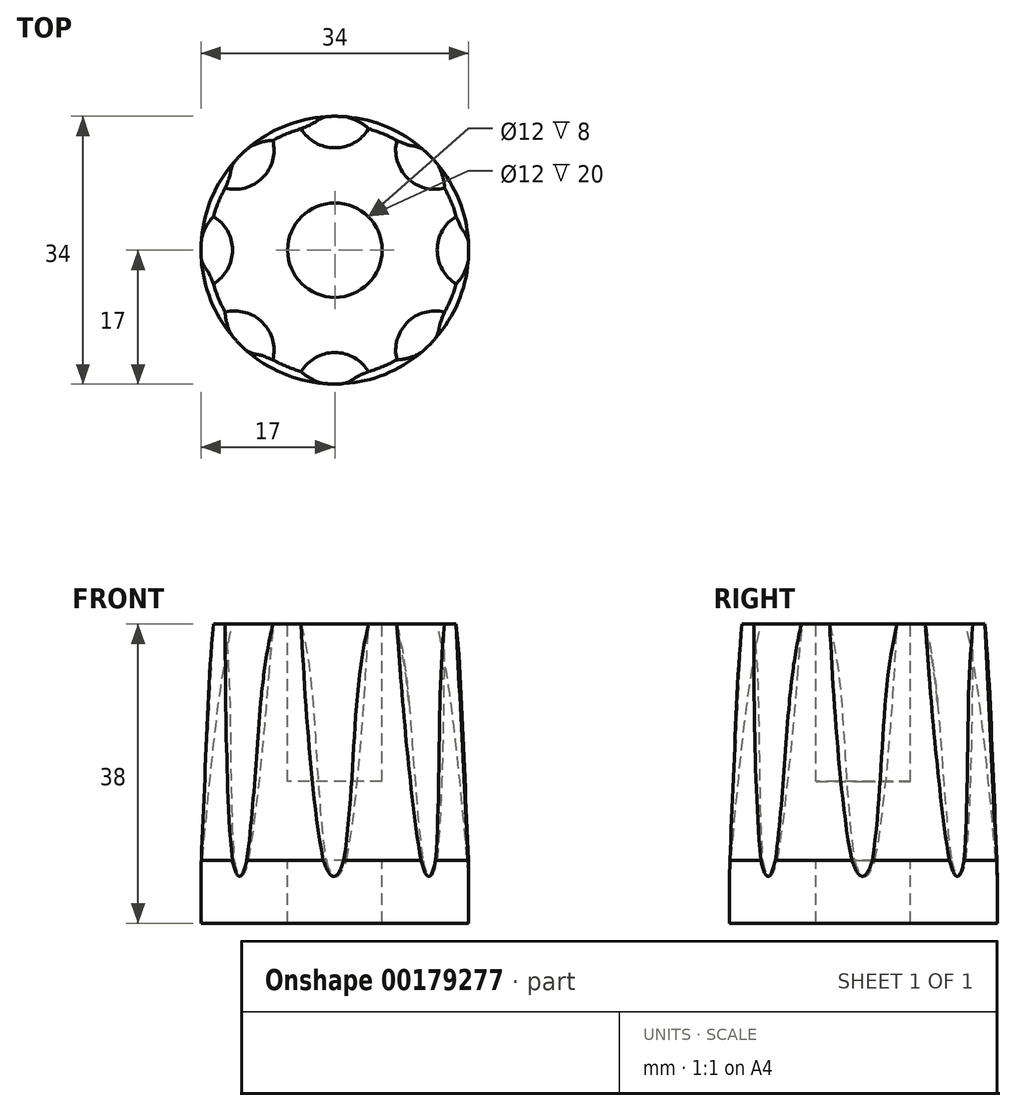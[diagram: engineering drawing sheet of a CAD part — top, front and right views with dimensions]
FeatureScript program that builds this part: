
annotation { "Feature Type Name" : "Feature", "Feature Type Description" : "" }
export const myFeature = defineFeature(function(context is Context, id is Id, definition is map)
    precondition{}
    {
        {
            var Q0;
            Q0=qCreatedBy(makeId("Front.planeOp"),FACE);
            var sketch = newSketch(context, id + "F0", { "sketchPlane" : qUnion([Q0])});
            skLineSegment(sketch, "E0", {"start": v(0, 8) * mm, "end": v(6, 8) * mm});
            skLineSegment(sketch, "E1", {"start": v(6, 8) * mm, "end": v(6, 0) * mm});
            skLineSegment(sketch, "E2", {"start": v(6, 0) * mm, "end": v(17, 0) * mm});
            skLineSegment(sketch, "E3", {"start": v(17, 0) * mm, "end": v(17, 8) * mm});
            skLineSegment(sketch, "E4", {"start": v(17, 8) * mm, "end": v(16, 38) * mm});
            skLineSegment(sketch, "E5", {"start": v(16, 38) * mm, "end": v(0, 38) * mm});
            skLineSegment(sketch, "E6", {"start": v(0, 38) * mm, "end": v(0, 8) * mm});
            skSolve(sketch);
        }
        {
            var Q0;
            Q0=makeQuery(id+"F0.imprint","IMPRINT",FACE,{"disambiguationData":[TD([[makeQuery(id+"F0.imprint","IMPRINT",EDGE,{"derivedFrom":sQuery(id+"F0.wireOp",EDGE,"E0")}),1.0]])]});
            var Q1;
            Q1=sQuery(id+"F0.wireOp",EDGE,"E6");
            revolve(context, id + "F1", {"entities" : qUnion([Q0]), "axis" : qUnion([Q1]), "revolveType" : RevolveType.FULL});
        }
        {
            var Q0;
            Q0=makeQuery(id+"F1.opRevolve","SWEPT_FACE",FACE,{"disambiguationData":[OSD([sQuery(id+"F0.wireOp",EDGE,"E5")])]});
            var sketch = newSketch(context, id + "F2", { "sketchPlane" : qUnion([Q0])});
            skCircle(sketch, "E7", {"center": v(18, 0) * mm, "radius": 5 * mm});
            skCircle(sketch, "E8.1.0", {"center": v(12.73, 12.73) * mm, "radius": 5 * mm});
            skCircle(sketch, "E8.2.0", {"center": v(0, 18) * mm, "radius": 5 * mm});
            skCircle(sketch, "E8.3.0", {"center": v(-12.73, 12.73) * mm, "radius": 5 * mm});
            skCircle(sketch, "E8.4.0", {"center": v(-18, 0) * mm, "radius": 5 * mm});
            skCircle(sketch, "E8.5.0", {"center": v(-12.73, -12.73) * mm, "radius": 5 * mm});
            skCircle(sketch, "E8.6.0", {"center": v(0, -18) * mm, "radius": 5 * mm});
            skCircle(sketch, "E8.7.0", {"center": v(12.73, -12.73) * mm, "radius": 5 * mm});
            skPoint(sketch, "E8.center", {"position": v(0, 0) * mm});
            skSolve(sketch);
        }
        {
            var Q0;
            Q0=makeQuery(id+"F1.opRevolve","SWEPT_FACE",FACE,{"disambiguationData":[OSD([sQuery(id+"F0.wireOp",EDGE,"E2")])]});
            var sketch = newSketch(context, id + "F3", { "sketchPlane" : qUnion([Q0])});
            skCircle(sketch, "E9", {"center": v(0, -25) * mm, "radius": 7.5 * mm});
            skCircle(sketch, "E10.1.0", {"center": v(17.68, -17.68) * mm, "radius": 7.5 * mm});
            skCircle(sketch, "E10.2.0", {"center": v(25, 0) * mm, "radius": 7.5 * mm});
            skCircle(sketch, "E10.3.0", {"center": v(17.68, 17.68) * mm, "radius": 7.5 * mm});
            skCircle(sketch, "E10.4.0", {"center": v(0, 25) * mm, "radius": 7.5 * mm});
            skCircle(sketch, "E10.5.0", {"center": v(-17.68, 17.68) * mm, "radius": 7.5 * mm});
            skCircle(sketch, "E10.6.0", {"center": v(-25, 0) * mm, "radius": 7.5 * mm});
            skCircle(sketch, "E10.7.0", {"center": v(-17.68, -17.68) * mm, "radius": 7.5 * mm});
            skPoint(sketch, "E10.center", {"position": v(0, 0) * mm});
            skSolve(sketch);
        }
        {
            var Q1;
            {var subQ0=sQuery(id+"F2.wireOp",EDGE,"E7");var subQ1=makeQuery(id+"F1.opRevolve","SWEPT_EDGE",EDGE,{"disambiguationData":[OSD([sQuery(id+"F0.wireOp",EDGE,"E4"),sQuery(id+"F0.wireOp",EDGE,"E5")])]});var subQ2=makeQuery(id+"F2.imprint","INTERSECT",VERTEX,{"disambiguationData":[OD(0.0)],"derivedFrom":[subQ1,subQ0]});Q1=makeQuery(id+"F2.imprint","IMPRINT",FACE,{"disambiguationData":[TD([[makeQuery(id+"F2.imprint","IMPRINT",EDGE,{"disambiguationData":[TD([[subQ2,1.0]])],"derivedFrom":subQ0}),1.0]])]});}
            var Q2;
            Q2=makeQuery(id+"F3.imprint","IMPRINT",FACE,{"disambiguationData":[TD([[makeQuery(id+"F3.imprint","IMPRINT",EDGE,{"derivedFrom":sQuery(id+"F3.wireOp",EDGE,"E10.2.0")}),1.0]])]});
            loft(context, id + "F4", {"sheetProfilesArray" : [{ "sheetProfileEntities" : qUnion([Q1]) }, { "sheetProfileEntities" : qUnion([Q2]) }]});
        }
        {
            var Q0;
            {var subQ0=sQuery(id+"F2.wireOp",EDGE,"E7");var subQ1=makeQuery(id+"F1.opRevolve","SWEPT_EDGE",EDGE,{"disambiguationData":[OSD([sQuery(id+"F0.wireOp",EDGE,"E4"),sQuery(id+"F0.wireOp",EDGE,"E5")])]});var subQ2=makeQuery(id+"F2.imprint","INTERSECT",VERTEX,{"disambiguationData":[OD(0.0)],"derivedFrom":[subQ1,subQ0]});Q0=makeQuery(id+"F4.opLoft","SWEPT_BODY",BODY,{"disambiguationData":[OSD([makeQuery(id+"F2.imprint","IMPRINT",FACE,{"disambiguationData":[TD([[makeQuery(id+"F2.imprint","IMPRINT",EDGE,{"disambiguationData":[TD([[subQ2,1.0]])],"derivedFrom":subQ0}),1.0]])]}),makeQuery(id+"F3.imprint","IMPRINT",FACE,{"disambiguationData":[TD([[makeQuery(id+"F3.imprint","IMPRINT",EDGE,{"derivedFrom":sQuery(id+"F3.wireOp",EDGE,"E10.2.0")}),1.0]])]})])]});}
            var Q1;
            Q1=sQuery(id+"F0.wireOp",EDGE,"E6");
            circularPattern(context, id + "F5", {"operationType" : NewBodyOperationType.REMOVE, "entities" : qUnion([Q0]), "axis" : qUnion([Q1]), "angle" : 45 * degree, "instanceCount" : 8});
        }
        {
            var Q0;
            Q0=makeQuery(id+"F1.opRevolve","SWEPT_FACE",FACE,{"disambiguationData":[OSD([sQuery(id+"F0.wireOp",EDGE,"E5")])]});
            var sketch = newSketch(context, id + "F6", { "sketchPlane" : qUnion([Q0])});
            skCircle(sketch, "E11", {"center": v(0, 0) * mm, "radius": 6 * mm});
            skFitSpline(sketch, "E12.0", {"points": [v(-13.93, -7.87) * mm, v(-13.72, -7.82) * mm, v(-13.5, -7.78) * mm, v(-13.3, -7.76) * mm, v(-13.08, -7.74) * mm, v(-12.87, -7.73) * mm, v(-12.66, -7.73) * mm, v(-12.44, -7.73) * mm, v(-12.23, -7.75) * mm, v(-12.02, -7.78) * mm, v(-11.8, -7.8) * mm, v(-11.6, -7.85) * mm, v(-11.39, -7.91) * mm, v(-11.18, -7.97) * mm, v(-10.98, -8.04) * mm, v(-10.78, -8.12) * mm, v(-10.58, -8.2) * mm, v(-10.4, -8.3) * mm, v(-10.2, -8.4) * mm, v(-10.02, -8.52) * mm, v(-9.84, -8.64) * mm, v(-9.67, -8.77) * mm, v(-9.5, -8.9) * mm, v(-9.34, -9.04) * mm, v(-9.2, -9.2) * mm, v(-9.04, -9.34) * mm, v(-8.9, -9.5) * mm, v(-8.77, -9.67) * mm, v(-8.64, -9.84) * mm, v(-8.52, -10.02) * mm, v(-8.4, -10.2) * mm, v(-8.3, -10.4) * mm, v(-8.2, -10.58) * mm, v(-8.12, -10.78) * mm, v(-8.04, -10.98) * mm, v(-7.97, -11.18) * mm, v(-7.91, -11.39) * mm, v(-7.85, -11.6) * mm, v(-7.8, -11.8) * mm, v(-7.78, -12.02) * mm, v(-7.75, -12.23) * mm, v(-7.73, -12.44) * mm, v(-7.73, -12.66) * mm, v(-7.73, -12.87) * mm, v(-7.74, -13.08) * mm, v(-7.76, -13.3) * mm, v(-7.78, -13.5) * mm, v(-7.82, -13.72) * mm, v(-7.87, -13.93) * mm]});
            skCircle(sketch, "E13.0", {"center": v(-12.73, -12.73) * mm, "radius": 5 * mm, "construction": true});
            skSolve(sketch);
        }
        {
            var Q0;
            Q0=makeQuery(id+"F6.imprint","IMPRINT",FACE,{"disambiguationData":[TD([[makeQuery(id+"F6.imprint","IMPRINT",EDGE,{"derivedFrom":sQuery(id+"F6.wireOp",EDGE,"E11")}),1.0]])]});
            var Q1;
            Q1=sQuery(id+"F6.wireOp",EDGE,"E11");
            extrude(context, id + "F7", {"entities" : qUnion([Q0]), "operationType" : NewBodyOperationType.REMOVE, "surfaceEntities" : qUnion([Q1]), "oppositeDirection" : true, "depth" : 20 * mm});
        }
    });
